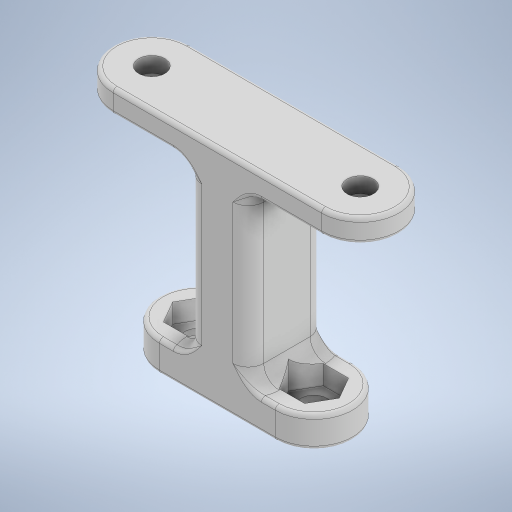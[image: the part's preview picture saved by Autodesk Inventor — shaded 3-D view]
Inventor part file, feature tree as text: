
AUTODESK INVENTOR PART (.ipt)
format: ipt  version: 2024.2 (Build 282272000, 272)  size: 423,936 bytes
history: native  units: mm
features: extrude x6, sketch x6, fillet x2
ambient origin geometry x8: Origin, YZ Plane, XZ Plane, XY Plane, X Axis, Y Axis, Z Axis, Center Point
bodies: Solid1 (feature_tree)
feature tree (14):
  extrude  "Extrusion1"  Depth=27.0mm
  extrude  "Extrusion2"  Depth=10.0mm TaperAngle=0.0deg
  extrude  "Extrusion3"  Depth=15.0mm
  extrude  "Extrusion4"  Depth=5.7mm
  extrude  "Extrusion5"  Depth=3.4mm
  extrude  "Extrusion6"  Depth=0.5mm
  fillet  "Fillet3"  Radius=1.0mm
  fillet  "Fillet2"  Radius=0.5mm
  sketch  "Sketch1"  dims[d0=3.4mm d1=27.0mm]
  sketch  "Sketch2"  dims[d2=10.0mm d3=3.0mm d4=0.0mm]
  sketch  "Sketch3"  dims[d5=22.1mm d6=0.0mm d7=15.0mm]
  sketch  "Sketch4"  dims[d8=4.0mm d9=0.0mm d10=5.7mm]
  sketch  "Sketch5"  dims[d11=2.5mm d12=0.0mm d13=3.4mm]
  sketch  "Sketch6"  dims[d14=2.0mm d15=0.0mm d16=5.1mm d17=1.0mm d18=0.0mm d20=0.5mm d22=8.0mm d23=2.0mm]
